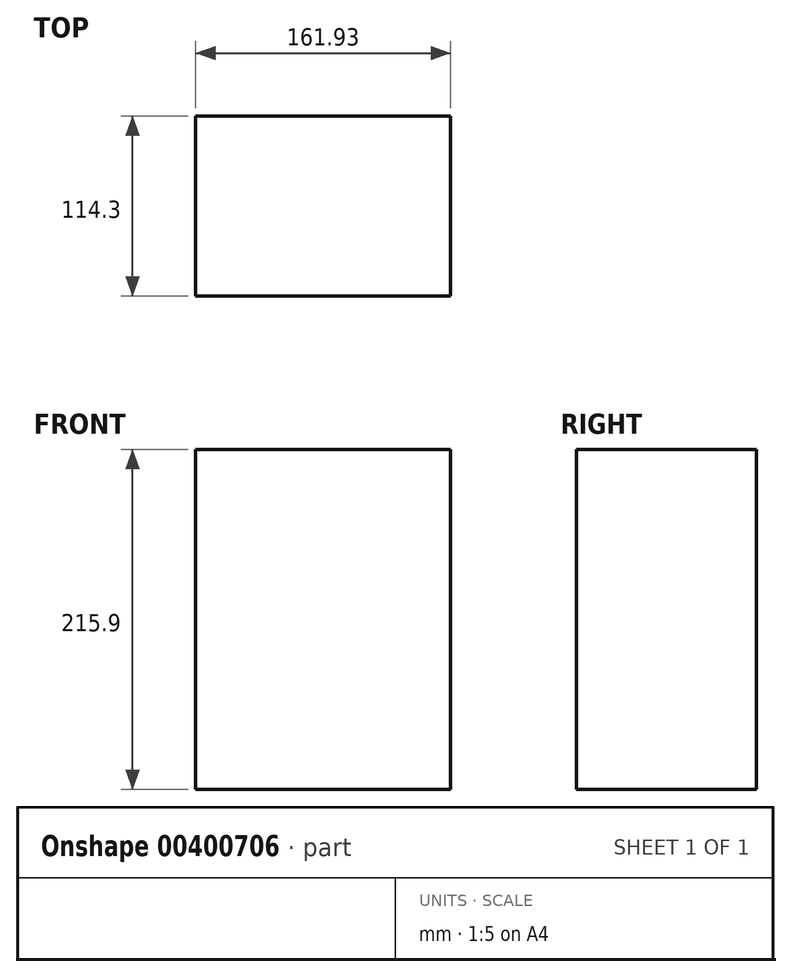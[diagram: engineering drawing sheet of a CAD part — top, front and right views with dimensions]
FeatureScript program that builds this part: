
annotation { "Feature Type Name" : "Feature", "Feature Type Description" : "" }
export const myFeature = defineFeature(function(context is Context, id is Id, definition is map)
    precondition{}
    {
        {
            var Q0;
            Q0=qCreatedBy(makeId("Front.planeOp"),FACE);
            var sketch = newSketch(context, id + "F0", { "sketchPlane" : qUnion([Q0])});
            skLineSegment(sketch, "E0.bottom", {"start": v(0, 0) * mm, "end": v(63.75, 0) * mm});
            skLineSegment(sketch, "E0.top", {"start": v(0, 85) * mm, "end": v(63.75, 85) * mm});
            skLineSegment(sketch, "E0.left", {"start": v(0, 0) * mm, "end": v(0, 85) * mm});
            skLineSegment(sketch, "E0.right", {"start": v(63.75, 0) * mm, "end": v(63.75, 85) * mm});
            skSolve(sketch);
        }
        {
            var Q0;
            Q0 = qSketchRegion(id + "F0", true);
            extrude(context, id + "F1", {"entities" : qUnion([Q0]), "oppositeDirection" : true, "depth" : 45 * mm});
        }
        {
            var Q0;
            Q0=makeQuery(id+"F1.opExtrude","SWEPT_BODY",BODY,{"disambiguationData":[OSD([sQuery(id+"F0.wireOp",EDGE,"E0.bottom"),sQuery(id+"F0.wireOp",EDGE,"E0.top"),sQuery(id+"F0.wireOp",EDGE,"E0.left"),sQuery(id+"F0.wireOp",EDGE,"E0.right")])]});
            var Q1;
            Q1=qCreatedBy(makeId("Origin.pointOp"),VERTEX);
            transform(context, id + "F2", {"entities" : qUnion([Q0]), "transformType" : TransformType.SCALE_UNIFORMLY, "scale" : 2.54, "scalePoint" : qUnion([Q1]), "makeCopy" : false});
        }
    });
